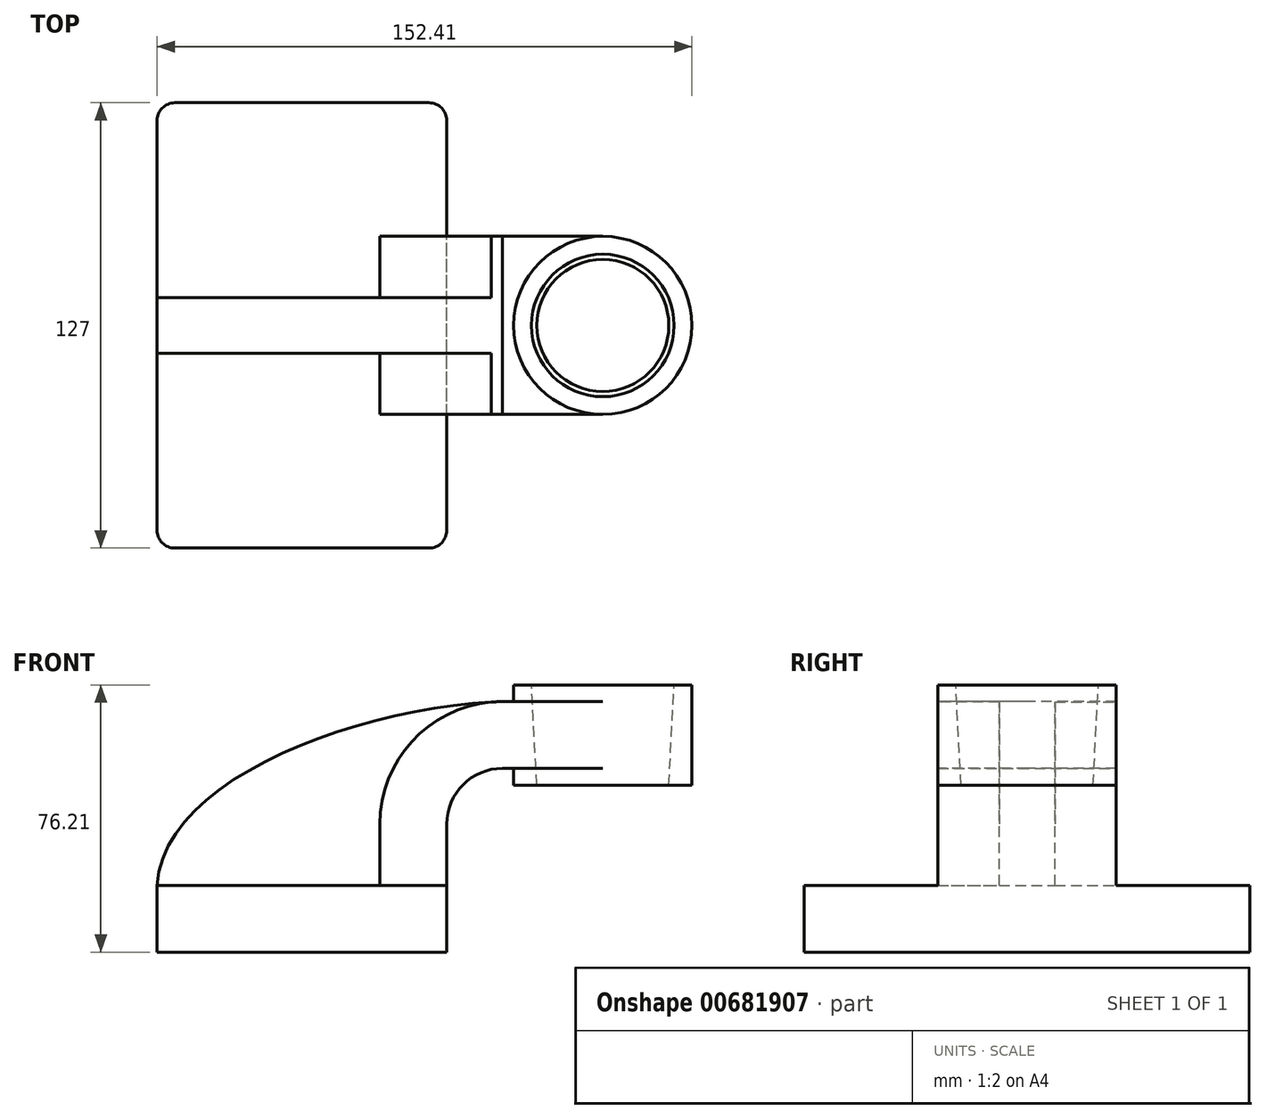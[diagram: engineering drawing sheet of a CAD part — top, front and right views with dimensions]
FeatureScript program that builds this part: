
annotation { "Feature Type Name" : "Feature", "Feature Type Description" : "" }
export const myFeature = defineFeature(function(context is Context, id is Id, definition is map)
    precondition{}
    {
        {
            var Q0;
            Q0=qCreatedBy(makeId("Front.planeOp"),FACE);
            var sketch = newSketch(context, id + "F0", { "sketchPlane" : qUnion([Q0])});
            skLineSegment(sketch, "E0.rect.bottom", {"start": v(-41.28, 9.52) * mm, "end": v(41.28, 9.52) * mm});
            skLineSegment(sketch, "E0.rect.top", {"start": v(-41.28, -9.52) * mm, "end": v(41.28, -9.52) * mm});
            skLineSegment(sketch, "E0.rect.left", {"start": v(-41.28, 9.52) * mm, "end": v(-41.28, -9.52) * mm});
            skLineSegment(sketch, "E0.rect.right", {"start": v(41.28, 9.52) * mm, "end": v(41.28, -9.52) * mm});
            skPoint(sketch, "E0.rect.middle", {"position": v(0, 0) * mm});
            skLineSegment(sketch, "E1", {"start": v(41.28, 9.52) * mm, "end": v(41.28, 27) * mm});
            skArc(sketch, "E2", {"start": v(41.28, 27) * mm, "mid": v(45.92, 38.23) * mm, "end": v(57.15, 42.88) * mm});
            skLineSegment(sketch, "E3", {"start": v(57.15, 42.88) * mm, "end": v(85.72, 42.88) * mm});
            skLineSegment(sketch, "E4.rect.bottom", {"start": v(60.32, 38.1) * mm, "end": v(111.12, 38.1) * mm});
            skLineSegment(sketch, "E4.rect.top", {"start": v(60.32, 66.68) * mm, "end": v(111.12, 66.68) * mm});
            skLineSegment(sketch, "E4.rect.left", {"start": v(60.32, 38.1) * mm, "end": v(60.32, 66.68) * mm});
            skLineSegment(sketch, "E4.rect.right", {"start": v(111.13, 38.1) * mm, "end": v(111.12, 66.68) * mm});
            skPoint(sketch, "E4.rect.middle", {"position": v(85.72, 52.39) * mm});
            skLineSegment(sketch, "E5.0", {"start": v(57.15, 61.93) * mm, "end": v(85.72, 61.93) * mm});
            skArc(sketch, "E5.1", {"start": v(22.23, 27) * mm, "mid": v(32.45, 51.7) * mm, "end": v(57.15, 61.93) * mm});
            skLineSegment(sketch, "E5.2", {"start": v(22.23, 9.52) * mm, "end": v(22.23, 27) * mm});
            skLineSegment(sketch, "E6", {"start": v(85.72, 38.1) * mm, "end": v(85.72, 66.68) * mm});
            skFitSpline(sketch, "E7", {"points": [v(-41.28, 9.53) * mm, v(57.15, 61.93) * mm], "startDerivative": vector(5.2, 92.34) * mm, "endDerivative": vector(120.92, 4.22) * mm});
            skSolve(sketch);
        }
        {
            var Q0;
            Q0=makeQuery(id+"F0.imprint","IMPRINT",FACE,{"disambiguationData":[TD([[makeQuery(id+"F0.imprint","IMPRINT",EDGE,{"derivedFrom":sQuery(id+"F0.wireOp",EDGE,"E0.rect.top")}),1.0]])]});
            extrude(context, id + "F1", {"entities" : qUnion([Q0]), "depth" : 127 * mm, "symmetric" : true});
        }
        {
            var Q0;
            {var subQ9=sQuery(id+"F0.wireOp",EDGE,"E1");Q0=makeQuery(id+"F0.imprint","IMPRINT",FACE,{"disambiguationData":[TD([[makeQuery(id+"F0.imprint","IMPRINT",EDGE,{"derivedFrom":subQ9}),1.0]])]});}
            var Q1;
            {var subQ0=sQuery(id+"F0.wireOp",EDGE,"E6");var subQ1=sQuery(id+"F0.wireOp",EDGE,"E3");var subQ2=makeQuery(id+"F0.imprint","INTERSECT",VERTEX,{"derivedFrom":[subQ1,subQ0]});Q1=makeQuery(id+"F0.imprint","IMPRINT",FACE,{"disambiguationData":[TD([[makeQuery(id+"F0.imprint","IMPRINT",EDGE,{"disambiguationData":[TD([[subQ2,1.0]])],"derivedFrom":subQ1}),1.0]])]});}
            extrude(context, id + "F2", {"entities" : qUnion([Q0, Q1]), "operationType" : NewBodyOperationType.ADD, "depth" : 50.8 * mm, "symmetric" : true});
        }
        {
            var Q0;
            {var subQ3=sQuery(id+"F0.wireOp",EDGE,"E5.2");Q0=makeQuery(id+"F0.imprint","IMPRINT",FACE,{"disambiguationData":[TD([[makeQuery(id+"F0.imprint","IMPRINT",EDGE,{"derivedFrom":subQ3}),1.0]])]});}
            extrude(context, id + "F3", {"entities" : qUnion([Q0]), "operationType" : NewBodyOperationType.ADD, "depth" : 15.88 * mm, "symmetric" : true});
        }
        {
            var Q0;
            {var subQ5=sQuery(id+"F0.wireOp",EDGE,"E4.rect.right");Q0=makeQuery(id+"F0.imprint","IMPRINT",FACE,{"disambiguationData":[TD([[makeQuery(id+"F0.imprint","IMPRINT",EDGE,{"derivedFrom":subQ5}),1.0]])]});}
            var Q1;
            Q1=sQuery(id+"F0.wireOp",EDGE,"E6");
            revolve(context, id + "F4", {"operationType" : NewBodyOperationType.ADD, "entities" : qUnion([Q0]), "axis" : qUnion([Q1]), "revolveType" : RevolveType.FULL});
        }
        {
            var Q0;
            Q0=makeQuery(id+"F1.opExtrude","CAP_EDGE",EDGE,{"disambiguationData":[OSD([sQuery(id+"F0.wireOp",EDGE,"E0.rect.right")])],"isStart":false});
            var Q1;
            Q1=makeQuery(id+"F1.opExtrude","CAP_EDGE",EDGE,{"disambiguationData":[OSD([sQuery(id+"F0.wireOp",EDGE,"E0.rect.left")])],"isStart":false});
            var Q2;
            Q2=makeQuery(id+"F1.opExtrude","CAP_EDGE",EDGE,{"disambiguationData":[OSD([sQuery(id+"F0.wireOp",EDGE,"E0.rect.right")])],"isStart":true});
            var Q3;
            Q3=makeQuery(id+"F1.opExtrude","CAP_EDGE",EDGE,{"disambiguationData":[OSD([sQuery(id+"F0.wireOp",EDGE,"E0.rect.left")])],"isStart":true});
            fillet(context, id + "F5", {"entities" : qUnion([Q0, Q1, Q2, Q3]), "radius" : 5.08 * mm, "tangentPropagation" : true, "allowEdgeOverflow" : false});
        }
        {
            var Q0;
            Q0=makeQuery(id+"F4.opRevolve","SWEPT_FACE",FACE,{"disambiguationData":[OSD([sQuery(id+"F0.wireOp",EDGE,"E4.rect.top")])]});
            var sketch = newSketch(context, id + "F6", { "sketchPlane" : qUnion([Q0])});
            skCircle(sketch, "E8", {"center": v(85.72, 0) * mm, "radius": 20.32 * mm});
            skSolve(sketch);
        }
        {
            var Q0;
            Q0 = qSketchRegion(id + "F6", true);
            extrude(context, id + "F7", {"entities" : qUnion([Q0]), "operationType" : NewBodyOperationType.REMOVE, "oppositeDirection" : true, "depth" : 50.8 * mm, "offsetDistance" : 25.4 * mm, "hasDraft" : true, "draftAngle" : 3 * degree, "draftPullDirection" : true});
        }
    });
